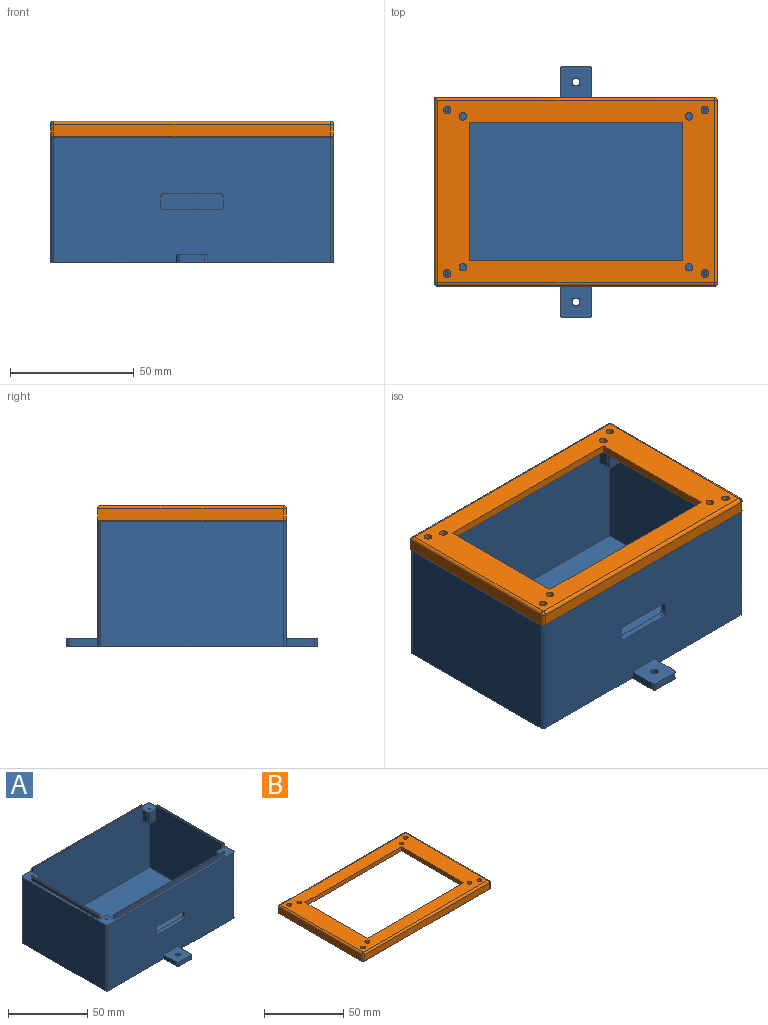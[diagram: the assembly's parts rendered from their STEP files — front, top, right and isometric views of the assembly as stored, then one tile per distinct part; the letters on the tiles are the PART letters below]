
ASSEMBLY  parts=2 mates=1
PART A: 89 faces, bbox 114.3x101.6x54 mm
  f0: plane 109.22x50.55mm, normal (0,1,0), area 5227.7mm2, adj f2,f3,f24,f26,f32,f45,f48,f50
  f1: plane 111.76x50.8mm, normal (0,-1,0), area 5477.2mm2, adj f6,f8,f10,f18,f31,f57,f58,f59
  f2: plane 71.12x50.55mm, normal (1,0,0), area 3461.8mm2, adj f0,f4,f27,f29,f32,f38,f39,f49
  f3: plane 71.12x50.55mm, normal (-1,0,0), area 3461.8mm2, adj f0,f4,f21,f23,f32,f42,f43,f47
  f4: plane 109.22x50.55mm, normal (0,-1,0), area 5387.6mm2, adj f2,f3,f20,f30,f32,f37,f39,f41
  f5: plane 12.7x12.7mm, normal (0,0,1), area 152.7mm2, adj f12,f13,f14,f15,f16,f53,f54
  f6: plane 12.7x12.7mm, normal (0,0,1), area 152.7mm2, adj f1,f8,f9,f10,f17,f55,f56
  f7: plane 73.66x50.8mm, normal (-1,0,0), area 3741.9mm2, adj f18,f31,f69,f70
  f8: plane 11.43x3.18mm, normal (-1,0,0), area 36.3mm2, adj f1,f6,f18,f55
  f9: plane 10.16x3.18mm, normal (0,-1,0), area 32.3mm2, adj f6,f18,f55,f56
  f10: plane 11.43x3.18mm, normal (1,0,0), area 36.3mm2, adj f1,f6,f18,f56
  f11: plane 73.66x50.8mm, normal (1,0,0), area 3741.9mm2, adj f18,f31,f71,f72
  f12: plane 111.76x50.8mm, normal (0,1,0), area 5637.1mm2, adj f5,f13,f16,f18,f31,f69,f72
  f13: plane 11.43x3.18mm, normal (1,0,0), area 36.3mm2, adj f5,f12,f18,f53
  f14: plane 10.16x3.18mm, normal (0,1,0), area 32.3mm2, adj f5,f18,f53,f54
  f15: cylinder r=1.59mm len=3.18mm, axis (0,0,1), area 31.7mm2, adj f5,f18
  f16: plane 11.43x3.18mm, normal (-1,0,0), area 36.3mm2, adj f5,f12,f18,f54
  f17: cylinder r=1.59mm len=3.18mm, axis (0,0,1), area 31.7mm2, adj f6,f18
  f18: plane 114.3x101.6mm, normal (0,0,-1), area 9013.6mm2, adj f1,f7,f8,f9,f10,f11,f12,f13
  f19: plane 97.54x2.92mm, normal (0,1,0), area 284.9mm2, adj f20,f30,f31,f86
  f20: plane 2.92x1.27mm, normal (1,0,0), area 3.7mm2, adj f4,f19,f31,f88
  f21: plane 2.92x1.27mm, normal (0,1,0), area 3.7mm2, adj f3,f22,f31,f81
  f22: plane 59.44x2.92mm, normal (1,0,0), area 173.6mm2, adj f21,f23,f31,f82
  f23: plane 2.92x1.27mm, normal (0,-1,0), area 3.7mm2, adj f3,f22,f31,f84
  f24: plane 2.92x1.27mm, normal (1,0,0), area 3.7mm2, adj f0,f25,f31,f77
  f25: plane 97.54x2.92mm, normal (0,-1,0), area 284.9mm2, adj f24,f26,f31,f78
  f26: plane 2.92x1.27mm, normal (-1,0,0), area 3.7mm2, adj f0,f25,f31,f80
  f27: plane 2.92x1.27mm, normal (0,-1,0), area 3.7mm2, adj f2,f28,f31,f73
  f28: plane 59.44x2.92mm, normal (-1,0,0), area 173.6mm2, adj f27,f29,f31,f74
  f29: plane 2.92x1.27mm, normal (0,1,0), area 3.7mm2, adj f2,f28,f31,f76
  f30: plane 2.92x1.27mm, normal (-1,0,0), area 3.7mm2, adj f4,f19,f31,f85
  f31: plane 114.3x76.2mm, normal (0,0,1), area 671.9mm2, adj f1,f7,f11,f12,f19,f20,f21,f22
  f32: plane 109.22x71.12mm, normal (0,0,1), area 7767.7mm2, adj f0,f2,f3,f4
  f33: plane 58.93x0.76mm, normal (0,0,1), area 44.9mm2, adj f73,f74,f75,f76
  f34: plane 58.93x0.76mm, normal (0,0,1), area 44.9mm2, adj f81,f82,f83,f84
  f35: plane 97.03x0.76mm, normal (0,0,1), area 73.9mm2, adj f77,f78,f79,f80
  f36: plane 97.03x0.76mm, normal (0,0,1), area 73.9mm2, adj f85,f86,f87,f88
  f37: plane 8.47x4.57mm, normal (1,0,0), area 38.7mm2, adj f4,f31,f39,f65
  f38: plane 8.47x4.57mm, normal (0,-1,0), area 38.7mm2, adj f2,f31,f39,f65
  f39: plane 5.84x5.84mm, normal (0,0,-1), area 32.5mm2, adj f2,f4,f37,f38,f40,f65
  f40: cylinder r=0.64mm len=8.47mm, axis (0,0,1), area 33.8mm2, adj f31,f39
  f41: plane 8.47x4.57mm, normal (-1,0,0), area 38.7mm2, adj f4,f31,f42,f68
  f42: plane 5.84x5.84mm, normal (0,0,-1), area 32.5mm2, adj f3,f4,f41,f43,f44,f68
  f43: plane 8.47x4.57mm, normal (0,-1,0), area 38.7mm2, adj f3,f31,f42,f68
  f44: cylinder r=0.64mm len=8.47mm, axis (0,0,1), area 33.8mm2, adj f31,f42
  f45: plane 8.47x4.57mm, normal (-1,0,0), area 38.7mm2, adj f0,f31,f48,f67
  f46: cylinder r=0.64mm len=8.47mm, axis (0,0,1), area 33.8mm2, adj f31,f48
  f47: plane 8.47x4.57mm, normal (0,1,0), area 38.7mm2, adj f3,f31,f48,f67
  f48: plane 5.84x5.84mm, normal (0,0,-1), area 32.5mm2, adj f0,f3,f45,f46,f47,f67
  f49: plane 8.47x4.57mm, normal (0,1,0), area 38.7mm2, adj f2,f31,f52,f66
  f50: plane 8.47x4.57mm, normal (1,0,0), area 38.7mm2, adj f0,f31,f52,f66
  f51: cylinder r=0.64mm len=8.47mm, axis (0,0,1), area 33.8mm2, adj f31,f52
  f52: plane 5.84x5.84mm, normal (0,0,-1), area 32.5mm2, adj f0,f2,f49,f50,f51,f66
  f53: cylinder r=1.27mm len=3.18mm, axis (0,0,-1), area 6.3mm2, adj f5,f13,f14,f18
  f54: cylinder r=1.27mm len=3.18mm, axis (0,0,1), area 6.3mm2, adj f5,f14,f16,f18
  f55: cylinder r=1.27mm len=3.18mm, axis (0,0,1), area 6.3mm2, adj f6,f8,f9,f18
  f56: cylinder r=1.27mm len=3.18mm, axis (0,0,-1), area 6.3mm2, adj f6,f9,f10,f18
  f57: plane 3.81x2.54mm, normal (1,0,0), area 9.7mm2, adj f0,f1,f61,f62
  f58: plane 22.86x2.54mm, normal (0,0,-1), area 58.1mm2, adj f0,f1,f61,f63
  f59: plane 22.86x2.54mm, normal (0,0,1), area 58.1mm2, adj f0,f1,f62,f64
  f60: plane 3.81x2.54mm, normal (-1,0,0), area 9.7mm2, adj f0,f1,f63,f64
  f61: cylinder r=1.27mm len=2.54mm, axis (0,1,0), area 5.1mm2, adj f0,f1,f57,f58
  f62: cylinder r=1.27mm len=2.54mm, axis (0,-1,0), area 5.1mm2, adj f0,f1,f57,f59
  f63: cylinder r=1.27mm len=2.54mm, axis (0,-1,0), area 5.1mm2, adj f0,f1,f58,f60
  f64: cylinder r=1.27mm len=2.54mm, axis (0,1,0), area 5.1mm2, adj f0,f1,f59,f60
  f65: cylinder r=1.27mm len=8.47mm, axis (0,0,-1), area 16.9mm2, adj f31,f37,f38,f39
  f66: cylinder r=1.27mm len=8.47mm, axis (0,0,-1), area 16.9mm2, adj f31,f49,f50,f52
  f67: cylinder r=1.27mm len=8.47mm, axis (0,0,-1), area 16.9mm2, adj f31,f45,f47,f48
  f68: cylinder r=1.27mm len=8.47mm, axis (0,0,-1), area 16.9mm2, adj f31,f41,f42,f43
  f69: cylinder r=1.27mm len=50.8mm, axis (0,0,1), area 101.3mm2, adj f7,f12,f18,f31
  f70: cylinder r=1.27mm len=50.8mm, axis (0,0,-1), area 101.3mm2, adj f1,f7,f18,f31
  f71: cylinder r=1.27mm len=50.8mm, axis (0,0,1), area 101.3mm2, adj f1,f11,f18,f31
  f72: cylinder r=1.27mm len=50.8mm, axis (0,0,-1), area 101.3mm2, adj f11,f12,f18,f31
  f73: cylinder r=0.25mm len=1.27mm, axis (1,0,0), area 0.4mm2, adj f27,f33,f74,f75
  f74: cylinder r=0.25mm len=59.44mm, axis (0,-1,0), area 23.6mm2, adj f28,f33,f73,f76
  f75: cylinder r=0.25mm len=59.44mm, axis (0,-1,0), area 23.6mm2, adj f2,f33,f73,f76
  f76: cylinder r=0.25mm len=1.27mm, axis (-1,0,0), area 0.4mm2, adj f29,f33,f74,f75
  f77: cylinder r=0.25mm len=1.27mm, axis (0,1,0), area 0.4mm2, adj f24,f35,f78,f79
  f78: cylinder r=0.25mm len=97.54mm, axis (1,0,0), area 38.8mm2, adj f25,f35,f77,f80
  f79: cylinder r=0.25mm len=97.54mm, axis (1,0,0), area 38.8mm2, adj f0,f35,f77,f80
  f80: cylinder r=0.25mm len=1.27mm, axis (0,-1,0), area 0.4mm2, adj f26,f35,f78,f79
  f81: cylinder r=0.25mm len=1.27mm, axis (-1,0,0), area 0.4mm2, adj f21,f34,f82,f83
  f82: cylinder r=0.25mm len=59.44mm, axis (0,1,0), area 23.6mm2, adj f22,f34,f81,f84
  f83: cylinder r=0.25mm len=59.44mm, axis (0,1,0), area 23.6mm2, adj f3,f34,f81,f84
  f84: cylinder r=0.25mm len=1.27mm, axis (1,0,0), area 0.4mm2, adj f23,f34,f82,f83
  f85: cylinder r=0.25mm len=1.27mm, axis (0,-1,0), area 0.4mm2, adj f30,f36,f86,f87
  f86: cylinder r=0.25mm len=97.54mm, axis (-1,0,0), area 38.8mm2, adj f19,f36,f85,f88
  f87: cylinder r=0.25mm len=97.54mm, axis (-1,0,0), area 38.8mm2, adj f4,f36,f85,f88
  f88: cylinder r=0.25mm len=1.27mm, axis (0,1,0), area 0.4mm2, adj f20,f36,f86,f87
PART B: 64 faces, bbox 114.5x76.4x6.4 mm
  f0: plane 55.88x3.18mm, normal (1,0,0), area 177.4mm2, adj f1,f15,f16,f17
  f1: plane 86.36x3.18mm, normal (0,-1,0), area 274.2mm2, adj f0,f2,f16,f17
  f2: plane 55.88x3.18mm, normal (-1,0,0), area 177.4mm2, adj f1,f15,f16,f17
  f3: plane 113.03x4.83mm, normal (0,1,0), area 545.5mm2, adj f4,f31,f35,f44
  f4: plane 74.93x4.83mm, normal (-1,0,0), area 361.6mm2, adj f3,f37,f40,f46
  f5: plane 111.76x4.83mm, normal (0,-1,0), area 539.4mm2, adj f34,f38,f40,f45
  f6: cylinder r=1.52mm len=3.18mm, axis (0,0,-1), area 30.4mm2, adj f16,f17
  f7: cylinder r=1.52mm len=3.18mm, axis (0,0,-1), area 30.4mm2, adj f16,f17
  f8: cylinder r=1.52mm len=3.18mm, axis (0,0,-1), area 30.4mm2, adj f16,f17
  f9: cylinder r=1.52mm len=3.18mm, axis (0,0,-1), area 30.4mm2, adj f16,f17
  f10: cylinder r=1.52mm len=6.1mm, axis (0,0,-1), area 58.4mm2, adj f16,f50
  f11: plane 73.66x4.83mm, normal (1,0,0), area 355.5mm2, adj f31,f33,f34,f41
  f12: cylinder r=1.52mm len=6.1mm, axis (0,0,-1), area 58.4mm2, adj f16,f49
  f13: cylinder r=1.52mm len=6.1mm, axis (0,0,-1), area 58.4mm2, adj f16,f63
  f14: cylinder r=1.52mm len=6.1mm, axis (0,0,-1), area 58.4mm2, adj f16,f48
  f15: plane 86.36x3.18mm, normal (0,1,0), area 274.2mm2, adj f0,f2,f16,f17
  f16: plane 111.76x73.66mm, normal (0,0,1), area 3348.1mm2, adj f0,f1,f2,f6,f7,f8,f9,f10
  f17: plane 111.76x73.66mm, normal (0,0,-1), area 3174.9mm2, adj f0,f1,f2,f6,f7,f8,f9,f15
  f18: plane 7.11x2.92mm, normal (1,0,0), area 20.8mm2, adj f17,f19,f29,f58
  f19: plane 97.54x2.92mm, normal (0,1,0), area 284.9mm2, adj f17,f18,f20,f56
  f20: plane 7.11x2.92mm, normal (-1,0,0), area 20.8mm2, adj f17,f19,f21,f54
  f21: plane 7.11x2.92mm, normal (0,1,0), area 20.8mm2, adj f17,f20,f22,f52
  f22: plane 59.44x2.92mm, normal (-1,0,0), area 173.6mm2, adj f17,f21,f23,f51
  f23: plane 7.11x2.92mm, normal (0,-1,0), area 20.8mm2, adj f17,f22,f24,f53
  f24: plane 7.11x2.92mm, normal (-1,0,0), area 20.8mm2, adj f17,f23,f25,f55
  f25: plane 97.54x2.92mm, normal (0,-1,0), area 284.9mm2, adj f17,f24,f26,f57
  f26: plane 7.11x2.92mm, normal (1,0,0), area 20.8mm2, adj f17,f25,f27,f59
  f27: plane 7.11x2.92mm, normal (0,-1,0), area 20.8mm2, adj f17,f26,f28,f61
  f28: plane 59.44x2.92mm, normal (1,0,0), area 173.6mm2, adj f17,f27,f29,f62
  f29: plane 7.11x2.92mm, normal (0,1,0), area 20.8mm2, adj f17,f18,f28,f60
  f30: plane 113.79x75.69mm, normal (0,0,-1), area 448.4mm2, adj f41,f42,f43,f44,f45,f46,f47,f48
  f31: cylinder r=1.27mm len=4.83mm, axis (0,0,1), area 9.6mm2, adj f3,f11,f32,f42
  f32: sphere r=1.27mm, area 2.5mm2, adj f31,f33,f35
  f33: cylinder r=1.27mm len=73.66mm, axis (0,-1,0), area 146.9mm2, adj f11,f16,f32,f36
  f34: cylinder r=1.27mm len=4.83mm, axis (0,0,-1), area 9.6mm2, adj f5,f11,f36,f43
  f35: cylinder r=1.27mm len=113.03mm, axis (1,0,0), area 224.6mm2, adj f3,f16,f32,f37
  f36: sphere r=1.27mm, area 2.5mm2, adj f33,f34,f38
  f37: cylinder r=1.27mm len=74.93mm, axis (0,1,0), area 148.6mm2, adj f4,f16,f35,f39
  f38: cylinder r=1.27mm len=111.76mm, axis (-1,0,0), area 223mm2, adj f5,f16,f36,f39
  f39: sphere r=1.27mm, area 2.5mm2, adj f37,f38,f40
  f40: cylinder r=1.27mm len=4.83mm, axis (0,0,1), area 9.6mm2, adj f4,f5,f39,f47
  f41: cylinder r=0.25mm len=73.66mm, axis (0,-1,0), area 29.4mm2, adj f11,f30,f42,f43
  f42: torus R=1.02mm, axis (0,0,-1), area 0.7mm2, adj f30,f31,f41,f44
  f43: torus R=1.02mm, axis (0,0,-1), area 0.7mm2, adj f30,f34,f41,f45
  f44: cylinder r=0.25mm len=113.03mm, axis (1,0,0), area 45.1mm2, adj f3,f30,f42,f46
  f45: cylinder r=0.25mm len=111.76mm, axis (-1,0,0), area 44.6mm2, adj f5,f30,f43,f47
  f46: cylinder r=0.25mm len=74.93mm, axis (0,1,0), area 29.9mm2, adj f4,f30,f44,f47
  f47: torus R=1.02mm, axis (0,0,-1), area 0.7mm2, adj f30,f40,f45,f46
  f48: torus R=1.78mm, axis (0,0,-1), area 4.1mm2, adj f14,f30
  f49: torus R=1.78mm, axis (0,0,-1), area 4.1mm2, adj f12,f30
  f50: torus R=1.78mm, axis (0,0,-1), area 4.1mm2, adj f10,f30
  f51: cylinder r=0.25mm len=59.94mm, axis (0,-1,0), area 23.8mm2, adj f22,f30,f52,f53
  f52: cylinder r=0.25mm len=7.37mm, axis (-1,0,0), area 2.8mm2, adj f21,f30,f51,f54
  f53: cylinder r=0.25mm len=7.37mm, axis (1,0,0), area 2.8mm2, adj f23,f30,f51,f55
  f54: cylinder r=0.25mm len=7.37mm, axis (0,-1,0), area 2.8mm2, adj f20,f30,f52,f56
  f55: cylinder r=0.25mm len=7.37mm, axis (0,-1,0), area 2.8mm2, adj f24,f30,f53,f57
  f56: cylinder r=0.25mm len=98.04mm, axis (-1,0,0), area 39mm2, adj f19,f30,f54,f58
  f57: cylinder r=0.25mm len=98.04mm, axis (1,0,0), area 39mm2, adj f25,f30,f55,f59
  f58: cylinder r=0.25mm len=7.37mm, axis (0,1,0), area 2.8mm2, adj f18,f30,f56,f60
  f59: cylinder r=0.25mm len=7.37mm, axis (0,1,0), area 2.8mm2, adj f26,f30,f57,f61
  f60: cylinder r=0.25mm len=7.37mm, axis (-1,0,0), area 2.8mm2, adj f29,f30,f58,f62
  f61: cylinder r=0.25mm len=7.37mm, axis (1,0,0), area 2.8mm2, adj f27,f30,f59,f62
  f62: cylinder r=0.25mm len=59.94mm, axis (0,1,0), area 23.8mm2, adj f28,f30,f60,f61
  f63: torus R=1.78mm, axis (0,0,-1), area 4.1mm2, adj f13,f30
PLACE A t=(-30.43,-17.34,-42.05)mm
PLACE B t=(-30.4,-17.36,8.75)mm
MATE planar A.f31 <-> B.f30  axis (0,0,1) through (-30.43,-17.34,5.58)mm
